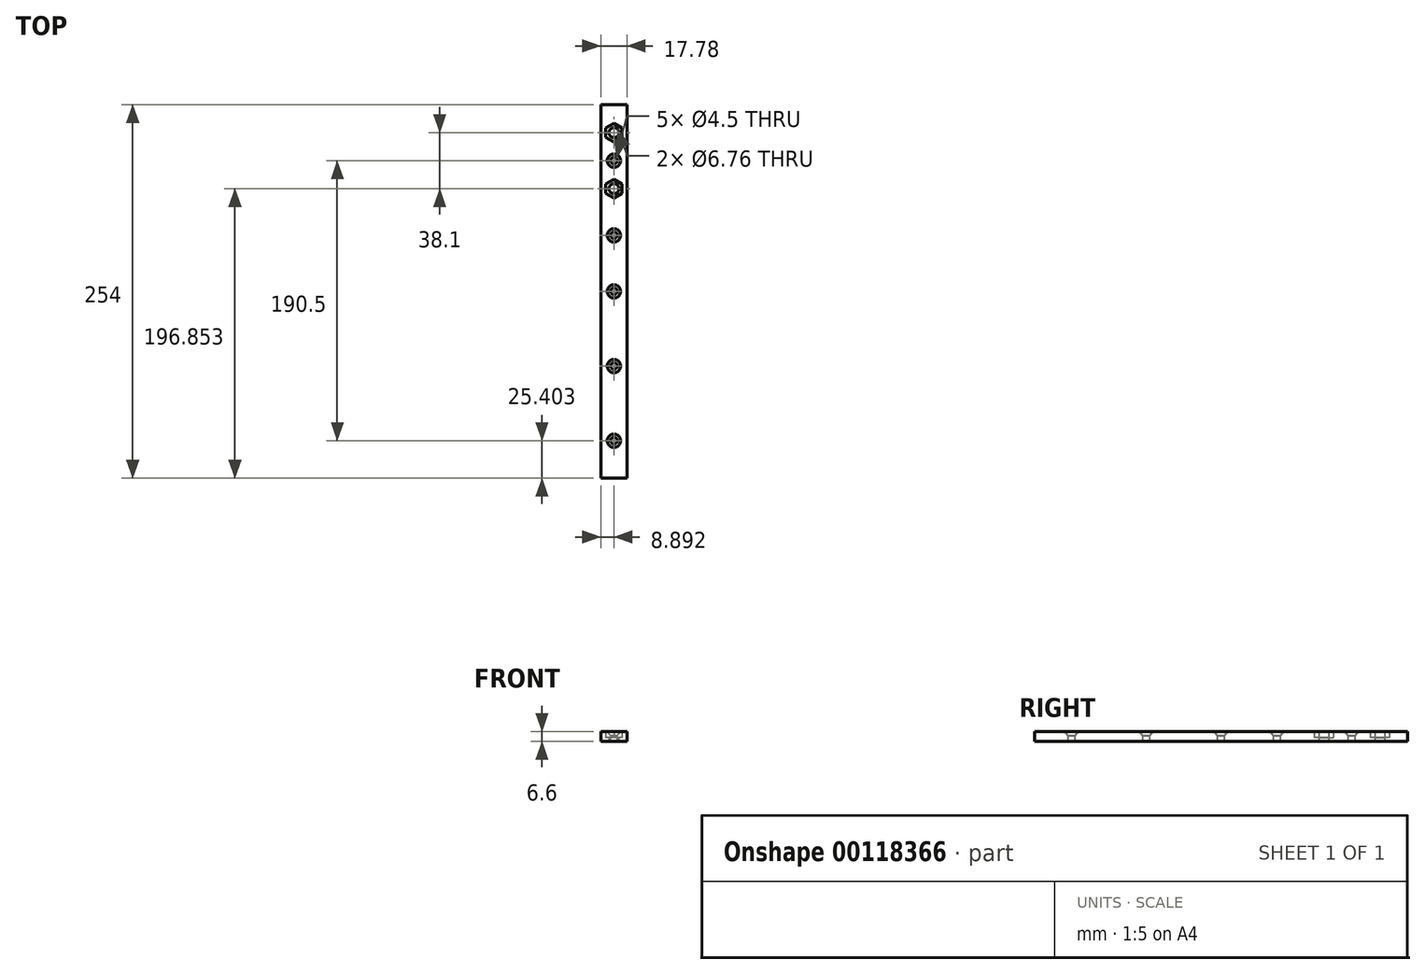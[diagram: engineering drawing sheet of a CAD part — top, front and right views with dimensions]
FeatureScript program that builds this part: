
annotation { "Feature Type Name" : "Feature", "Feature Type Description" : "" }
export const myFeature = defineFeature(function(context is Context, id is Id, definition is map)
    precondition{}
    {
        {
            var Q0;
            Q0=qCreatedBy(makeId("Top.planeOp"),FACE);
            var sketch = newSketch(context, id + "F0", { "sketchPlane" : qUnion([Q0])});
            skLineSegment(sketch, "E0.bottom", {"start": v(-5.89, 167.12) * mm, "end": v(11.9, 167.12) * mm});
            skLineSegment(sketch, "E0.top", {"start": v(-5.89, -86.88) * mm, "end": v(11.9, -86.88) * mm});
            skLineSegment(sketch, "E0.left", {"start": v(-5.89, 167.12) * mm, "end": v(-5.89, -86.88) * mm});
            skLineSegment(sketch, "E0.right", {"start": v(11.9, 167.12) * mm, "end": v(11.9, -86.88) * mm});
            skCircle(sketch, "E1.cCircle", {"center": v(3, 148.07) * mm, "radius": 5.59 * mm, "construction": true});
            skPoint(sketch, "E1.cCircle.centerSnap0", {"position": v(3, 167.12) * mm});
            skLineSegment(sketch, "E1.0", {"start": v(8.59, 151.3) * mm, "end": v(8.59, 144.85) * mm});
            skLineSegment(sketch, "E1.1", {"start": v(8.59, 144.85) * mm, "end": v(3, 141.62) * mm});
            skLineSegment(sketch, "E1.2", {"start": v(3, 141.62) * mm, "end": v(-2.59, 144.85) * mm});
            skLineSegment(sketch, "E1.3", {"start": v(-2.59, 144.85) * mm, "end": v(-2.59, 151.3) * mm});
            skLineSegment(sketch, "E1.4", {"start": v(-2.59, 151.3) * mm, "end": v(3, 154.53) * mm});
            skLineSegment(sketch, "E1.5", {"start": v(3, 154.53) * mm, "end": v(8.59, 151.3) * mm});
            skPoint(sketch, "E1.0.midPoint", {"position": v(8.59, 148.07) * mm});
            skCircle(sketch, "E2.cCircle", {"center": v(3, 109.97) * mm, "radius": 5.59 * mm, "construction": true});
            skLineSegment(sketch, "E2.0", {"start": v(8.59, 106.75) * mm, "end": v(3, 103.52) * mm});
            skLineSegment(sketch, "E2.1", {"start": v(3, 103.52) * mm, "end": v(-2.59, 106.75) * mm});
            skLineSegment(sketch, "E2.2", {"start": v(-2.59, 106.75) * mm, "end": v(-2.59, 113.2) * mm});
            skLineSegment(sketch, "E2.3", {"start": v(-2.59, 113.2) * mm, "end": v(3, 116.43) * mm});
            skLineSegment(sketch, "E2.4", {"start": v(3, 116.43) * mm, "end": v(8.59, 113.2) * mm});
            skLineSegment(sketch, "E2.5", {"start": v(8.59, 113.2) * mm, "end": v(8.59, 106.75) * mm});
            skPoint(sketch, "E2.0.midPoint", {"position": v(5.8, 105.13) * mm});
            skCircle(sketch, "E3", {"center": v(3, 148.07) * mm, "radius": 3.38 * mm});
            skCircle(sketch, "E4", {"center": v(3, 109.97) * mm, "radius": 3.38 * mm});
            skSolve(sketch);
        }
        {
            var Q0;
            Q0=makeQuery(id+"F0.imprint","IMPRINT",FACE,{"disambiguationData":[TD([[makeQuery(id+"F0.imprint","IMPRINT",EDGE,{"derivedFrom":sQuery(id+"F0.wireOp",EDGE,"E0.bottom")}),-1.0]])]});
            extrude(context, id + "F1", {"entities" : qUnion([Q0]), "depth" : 6.6 * mm});
        }
        {
            var Q0;
            Q0=makeQuery(id+"F0.imprint","IMPRINT",FACE,{"disambiguationData":[TD([[makeQuery(id+"F0.imprint","IMPRINT",EDGE,{"derivedFrom":sQuery(id+"F0.wireOp",EDGE,"E2.0")}),-1.0]])]});
            var Q1;
            Q1=makeQuery(id+"F0.imprint","IMPRINT",FACE,{"disambiguationData":[TD([[makeQuery(id+"F0.imprint","IMPRINT",EDGE,{"derivedFrom":sQuery(id+"F0.wireOp",EDGE,"E1.0")}),-1.0]])]});
            extrude(context, id + "F2", {"entities" : qUnion([Q0, Q1]), "operationType" : NewBodyOperationType.ADD, "depth" : 2.54 * mm});
        }
        {
            var Q0;
            Q0=makeQuery(id+"F1.opExtrude","CAP_FACE",FACE,{"disambiguationData":[OSD([sQuery(id+"F0.wireOp",EDGE,"E0.bottom"),sQuery(id+"F0.wireOp",EDGE,"E0.top"),sQuery(id+"F0.wireOp",EDGE,"E0.left"),sQuery(id+"F0.wireOp",EDGE,"E0.right"),sQuery(id+"F0.wireOp",EDGE,"E1.0"),sQuery(id+"F0.wireOp",EDGE,"E1.1"),sQuery(id+"F0.wireOp",EDGE,"E1.2"),sQuery(id+"F0.wireOp",EDGE,"E1.3"),sQuery(id+"F0.wireOp",EDGE,"E1.4"),sQuery(id+"F0.wireOp",EDGE,"E1.5"),sQuery(id+"F0.wireOp",EDGE,"E2.0"),sQuery(id+"F0.wireOp",EDGE,"E2.1"),sQuery(id+"F0.wireOp",EDGE,"E2.2"),sQuery(id+"F0.wireOp",EDGE,"E2.3"),sQuery(id+"F0.wireOp",EDGE,"E2.4"),sQuery(id+"F0.wireOp",EDGE,"E2.5")])],"isStart":false});
            var sketch = newSketch(context, id + "F3", { "sketchPlane" : qUnion([Q0])});
            skPoint(sketch, "E5", {"position": v(3, -61.48) * mm});
            skPoint(sketch, "E5.positionSnap0", {"position": v(3, -86.88) * mm});
            skPoint(sketch, "E6", {"position": v(3, -10.68) * mm});
            skPoint(sketch, "E7", {"position": v(3, 40.12) * mm});
            skPoint(sketch, "E8", {"position": v(3, 129.02) * mm});
            skPoint(sketch, "E9", {"position": v(3, 78.22) * mm});
            skSolve(sketch);
        }
        {
            var Q0;
            Q0=sQuery(id+"F3.wireOp",VERTEX,"E8");
            var Q1;
            Q1=sQuery(id+"F3.wireOp",VERTEX,"E9");
            var Q2;
            Q2=sQuery(id+"F3.wireOp",VERTEX,"E7");
            var Q3;
            Q3=sQuery(id+"F3.wireOp",VERTEX,"E6");
            var Q4;
            Q4=sQuery(id+"F3.wireOp",VERTEX,"E5");
            var Q5;
            Q5=makeQuery(id+"F1.opExtrude","SWEPT_BODY",BODY,{"disambiguationData":[OSD([sQuery(id+"F0.wireOp",EDGE,"E0.bottom"),sQuery(id+"F0.wireOp",EDGE,"E0.top"),sQuery(id+"F0.wireOp",EDGE,"E0.left"),sQuery(id+"F0.wireOp",EDGE,"E0.right"),sQuery(id+"F0.wireOp",EDGE,"E1.0"),sQuery(id+"F0.wireOp",EDGE,"E1.1"),sQuery(id+"F0.wireOp",EDGE,"E1.2"),sQuery(id+"F0.wireOp",EDGE,"E1.3"),sQuery(id+"F0.wireOp",EDGE,"E1.4"),sQuery(id+"F0.wireOp",EDGE,"E1.5"),sQuery(id+"F0.wireOp",EDGE,"E2.0"),sQuery(id+"F0.wireOp",EDGE,"E2.1"),sQuery(id+"F0.wireOp",EDGE,"E2.2"),sQuery(id+"F0.wireOp",EDGE,"E2.3"),sQuery(id+"F0.wireOp",EDGE,"E2.4"),sQuery(id+"F0.wireOp",EDGE,"E2.5")])]});
            hole(context, id + "F4", {"style" : HoleStyle.C_SINK, "endStyle" : HoleEndStyle.THROUGH, "standardTappedOrClearance" : lookupTablePath({ "standard" : "ANSI", "fit" : "Normal (ASME)", "size" : "#8", "type" : "Clearance" }), "standardBlindInLast" : lookupTablePath({ "fit" : "Free", "standard" : "ANSI", "size" : "#8", "type" : "Clearance" }), "holeDiameter" : 4.5 * mm, "cSinkDiameter" : 9.12 * mm, "cSinkAngle" : 82 * degree, "locations" : qUnion([Q0, Q1, Q2, Q3, Q4]), "scope" : qUnion([Q5]), "isTappedThrough" : true});
        }
    });
